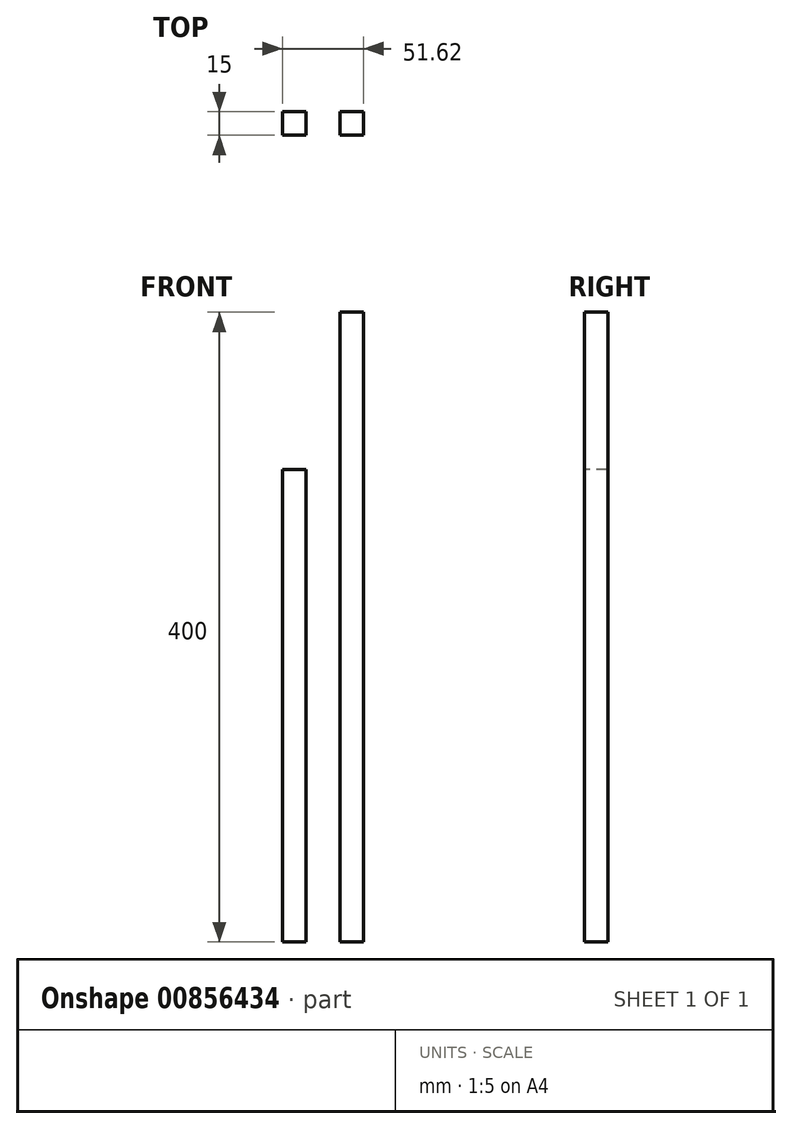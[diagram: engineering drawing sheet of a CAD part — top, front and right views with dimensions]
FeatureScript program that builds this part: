
annotation { "Feature Type Name" : "Feature", "Feature Type Description" : "" }
export const myFeature = defineFeature(function(context is Context, id is Id, definition is map)
    precondition{}
    {
        {
            var Q0;
            Q0=qCreatedBy(makeId("Top.planeOp"),FACE);
            var sketch = newSketch(context, id + "F0", { "sketchPlane" : qUnion([Q0])});
            skLineSegment(sketch, "E0.bottom", {"start": v(-7.5, 7.5) * mm, "end": v(7.5, 7.5) * mm});
            skLineSegment(sketch, "E0.top", {"start": v(-7.5, -7.5) * mm, "end": v(7.5, -7.5) * mm});
            skLineSegment(sketch, "E0.left", {"start": v(-7.5, 7.5) * mm, "end": v(-7.5, -7.5) * mm});
            skLineSegment(sketch, "E0.right", {"start": v(7.5, 7.5) * mm, "end": v(7.5, -7.5) * mm});
            skSolve(sketch);
        }
        {
            var Q0;
            Q0=makeQuery(id+"F0.imprint","IMPRINT",FACE,{"disambiguationData":[TD([[makeQuery(id+"F0.imprint","IMPRINT",EDGE,{"derivedFrom":sQuery(id+"F0.wireOp",EDGE,"E0.bottom")}),-1.0]])]});
            extrude(context, id + "F1", {"entities" : qUnion([Q0]), "depth" : 400 * mm, "offsetDistance" : 25.4 * mm});
        }
        {
            var Q0;
            Q0=makeQuery(id+"F1.opExtrude","SWEPT_BODY",BODY,{"disambiguationData":[OSD([sQuery(id+"F0.wireOp",EDGE,"E0.bottom"),sQuery(id+"F0.wireOp",EDGE,"E0.top"),sQuery(id+"F0.wireOp",EDGE,"E0.left"),sQuery(id+"F0.wireOp",EDGE,"E0.right")])]});
            transform(context, id + "F2", {"entities" : qUnion([Q0]), "transformType" : TransformType.TRANSLATION_3D, "dx" : -45.97 * mm, "dy" : 0 * mm, "dz" : 0 * mm, "makeCopy" : true});
        }
        {
            var Q0;
            Q0=makeQuery(id+"F2.opPattern","COPY",BODY,{"derivedFrom":makeQuery(id+"F1.opExtrude","SWEPT_BODY",BODY,{"disambiguationData":[OSD([sQuery(id+"F0.wireOp",EDGE,"E0.bottom"),sQuery(id+"F0.wireOp",EDGE,"E0.top"),sQuery(id+"F0.wireOp",EDGE,"E0.left"),sQuery(id+"F0.wireOp",EDGE,"E0.right")])]}),"instanceName":"1"});
            deleteBodies(context, id + "F3", {"entities" : qUnion([Q0])});
        }
        {
            var Q0;
            Q0=qCreatedBy(makeId("Top.planeOp"),FACE);
            var sketch = newSketch(context, id + "F4", { "sketchPlane" : qUnion([Q0])});
            skLineSegment(sketch, "E1.bottom", {"start": v(-44.12, 7.5) * mm, "end": v(-29.12, 7.5) * mm});
            skLineSegment(sketch, "E1.top", {"start": v(-44.12, -7.5) * mm, "end": v(-29.12, -7.5) * mm});
            skLineSegment(sketch, "E1.left", {"start": v(-44.12, 7.5) * mm, "end": v(-44.12, -7.5) * mm});
            skLineSegment(sketch, "E1.right", {"start": v(-29.12, 7.5) * mm, "end": v(-29.12, -7.5) * mm});
            skSolve(sketch);
        }
        {
            var Q0;
            Q0=makeQuery(id+"F4.imprint","IMPRINT",FACE,{"disambiguationData":[TD([[makeQuery(id+"F4.imprint","IMPRINT",EDGE,{"derivedFrom":sQuery(id+"F4.wireOp",EDGE,"E1.bottom")}),-1.0]])]});
            extrude(context, id + "F5", {"entities" : qUnion([Q0]), "depth" : 300 * mm, "offsetDistance" : 25.4 * mm});
        }
    });
